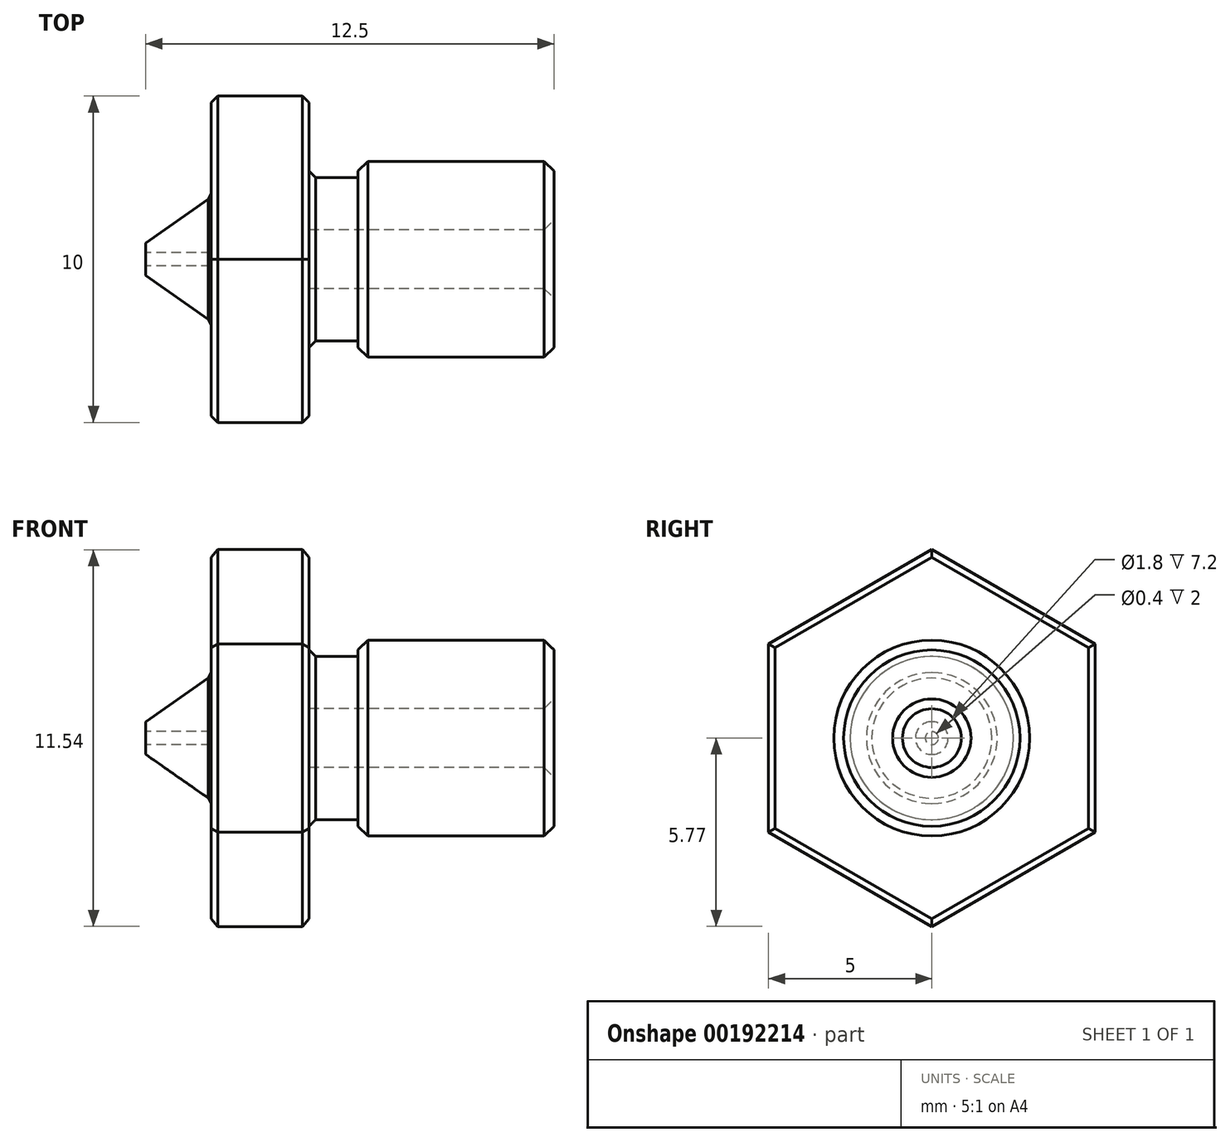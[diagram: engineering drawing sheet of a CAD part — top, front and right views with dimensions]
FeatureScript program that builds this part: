
annotation { "Feature Type Name" : "Feature", "Feature Type Description" : "" }
export const myFeature = defineFeature(function(context is Context, id is Id, definition is map)
    precondition{}
    {
        {
            var Q0;
            Q0=qCreatedBy(makeId("Front.planeOp"),FACE);
            var sketch = newSketch(context, id + "F0", { "sketchPlane" : qUnion([Q0])});
            skLineSegment(sketch, "E0", {"start": v(0, 0) * mm, "end": v(27.63, 0) * mm, "construction": true});
            skLineSegment(sketch, "E1", {"start": v(0, 0.5) * mm, "end": v(0, 0.2) * mm});
            skLineSegment(sketch, "E2", {"start": v(0, 0.2) * mm, "end": v(3, 0.2) * mm});
            skLineSegment(sketch, "E3", {"start": v(3, 0.2) * mm, "end": v(3.7, 0.9) * mm});
            skLineSegment(sketch, "E4", {"start": v(3.7, 0.9) * mm, "end": v(12.5, 0.9) * mm});
            skLineSegment(sketch, "E5", {"start": v(12.5, 0.9) * mm, "end": v(12.5, 3) * mm});
            skLineSegment(sketch, "E6", {"start": v(12.5, 3) * mm, "end": v(6.5, 3) * mm});
            skLineSegment(sketch, "E7", {"start": v(0, 0.5) * mm, "end": v(2, 1.9) * mm});
            skLineSegment(sketch, "E8", {"start": v(2, 1.9) * mm, "end": v(2, 5) * mm});
            skLineSegment(sketch, "E9", {"start": v(2, 5) * mm, "end": v(5, 5) * mm});
            skLineSegment(sketch, "E10", {"start": v(5, 5) * mm, "end": v(5, 2.5) * mm});
            skLineSegment(sketch, "E11", {"start": v(5, 2.5) * mm, "end": v(6.5, 2.5) * mm});
            skLineSegment(sketch, "E12", {"start": v(6.5, 2.5) * mm, "end": v(6.5, 3) * mm});
            skSolve(sketch);
        }
        {
            var Q0;
            Q0 = qSketchRegion(id + "F0", true);
            var Q1;
            Q1=sQuery(id+"F0.wireOp",EDGE,"E0");
            revolve(context, id + "F1", {"entities" : qUnion([Q0]), "axis" : qUnion([Q1]), "revolveType" : RevolveType.FULL});
        }
        {
            var Q0;
            Q0=makeQuery(id+"F1.opRevolve","SWEPT_EDGE",EDGE,{"disambiguationData":[OSD([sQuery(id+"F0.wireOp",EDGE,"E4"),sQuery(id+"F0.wireOp",EDGE,"E5")])]});
            var Q1;
            Q1=makeQuery(id+"F1.opRevolve","SWEPT_EDGE",EDGE,{"disambiguationData":[OSD([sQuery(id+"F0.wireOp",EDGE,"E5"),sQuery(id+"F0.wireOp",EDGE,"E6")])]});
            var Q2;
            Q2=makeQuery(id+"F1.opRevolve","SWEPT_EDGE",EDGE,{"disambiguationData":[OSD([sQuery(id+"F0.wireOp",EDGE,"E6"),sQuery(id+"F0.wireOp",EDGE,"E12")])]});
            chamfer(context, id + "F2", {"entities" : qUnion([Q0, Q1, Q2]), "width" : 0.3 * mm, "tangentPropagation" : true});
        }
        {
            var Q0;
            Q0=makeQuery(id+"F1.opRevolve","SWEPT_FACE",FACE,{"disambiguationData":[OSD([sQuery(id+"F0.wireOp",EDGE,"E8")])]});
            var sketch = newSketch(context, id + "F3", { "sketchPlane" : qUnion([Q0])});
            skCircle(sketch, "E13.cCircle", {"center": v(0, 0) * mm, "radius": 5 * mm, "construction": true});
            skLineSegment(sketch, "E13.0", {"start": v(5, 2.89) * mm, "end": v(5, -2.89) * mm});
            skLineSegment(sketch, "E13.1", {"start": v(5, -2.89) * mm, "end": v(0, -5.77) * mm});
            skLineSegment(sketch, "E13.2", {"start": v(0, -5.77) * mm, "end": v(-5, -2.89) * mm});
            skLineSegment(sketch, "E13.3", {"start": v(-5, -2.89) * mm, "end": v(-5, 2.89) * mm});
            skLineSegment(sketch, "E13.4", {"start": v(-5, 2.89) * mm, "end": v(0, 5.77) * mm});
            skLineSegment(sketch, "E13.5", {"start": v(0, 5.77) * mm, "end": v(5, 2.89) * mm});
            skPoint(sketch, "E13.0.midPoint", {"position": v(5, 0) * mm});
            skSolve(sketch);
        }
        {
            var Q0;
            Q0 = qSketchRegion(id + "F3", true);
            var Q1;
            Q1=makeQuery(id+"F1.opRevolve","SWEPT_FACE",FACE,{"disambiguationData":[OSD([sQuery(id+"F0.wireOp",EDGE,"E10")])]});
            extrude(context, id + "F4", {"entities" : qUnion([Q0]), "operationType" : NewBodyOperationType.ADD, "endBound" : BoundingType.UP_TO_SURFACE, "oppositeDirection" : true, "endBoundEntityFace" : qUnion([Q1]), "depth" : 25 * mm});
        }
        {
            var Q0;
            Q0=makeQuery(id+"F4.boolean.opBoolean","MERGE",FACE,{"derivedFrom":[makeQuery(id+"F1.opRevolve","SWEPT_FACE",FACE,{"disambiguationData":[OSD([sQuery(id+"F0.wireOp",EDGE,"E8")])]}),makeQuery(id+"F4.opExtrude","CAP_FACE",FACE,{"disambiguationData":[OSD([sQuery(id+"F3.wireOp",EDGE,"E13.0"),sQuery(id+"F3.wireOp",EDGE,"E13.1"),sQuery(id+"F3.wireOp",EDGE,"E13.2"),sQuery(id+"F3.wireOp",EDGE,"E13.3"),sQuery(id+"F3.wireOp",EDGE,"E13.4"),sQuery(id+"F3.wireOp",EDGE,"E13.5")])],"isStart":true})]});
            var Q1;
            {var subQ0=sQuery(id+"F0.wireOp",EDGE,"E10");Q1=makeQuery(id+"F4.boolean.opBoolean","MERGE",FACE,{"derivedFrom":[makeQuery(id+"F1.opRevolve","SWEPT_FACE",FACE,{"disambiguationData":[OSD([subQ0])]}),makeQuery(id+"F4.opExtrude","CAP_FACE",FACE,{"disambiguationData":[OSD([subQ0])],"isStart":false})]});}
            chamfer(context, id + "F5", {"entities" : qUnion([Q0, Q1]), "width" : 0.2 * mm, "tangentPropagation" : true});
        }
    });
